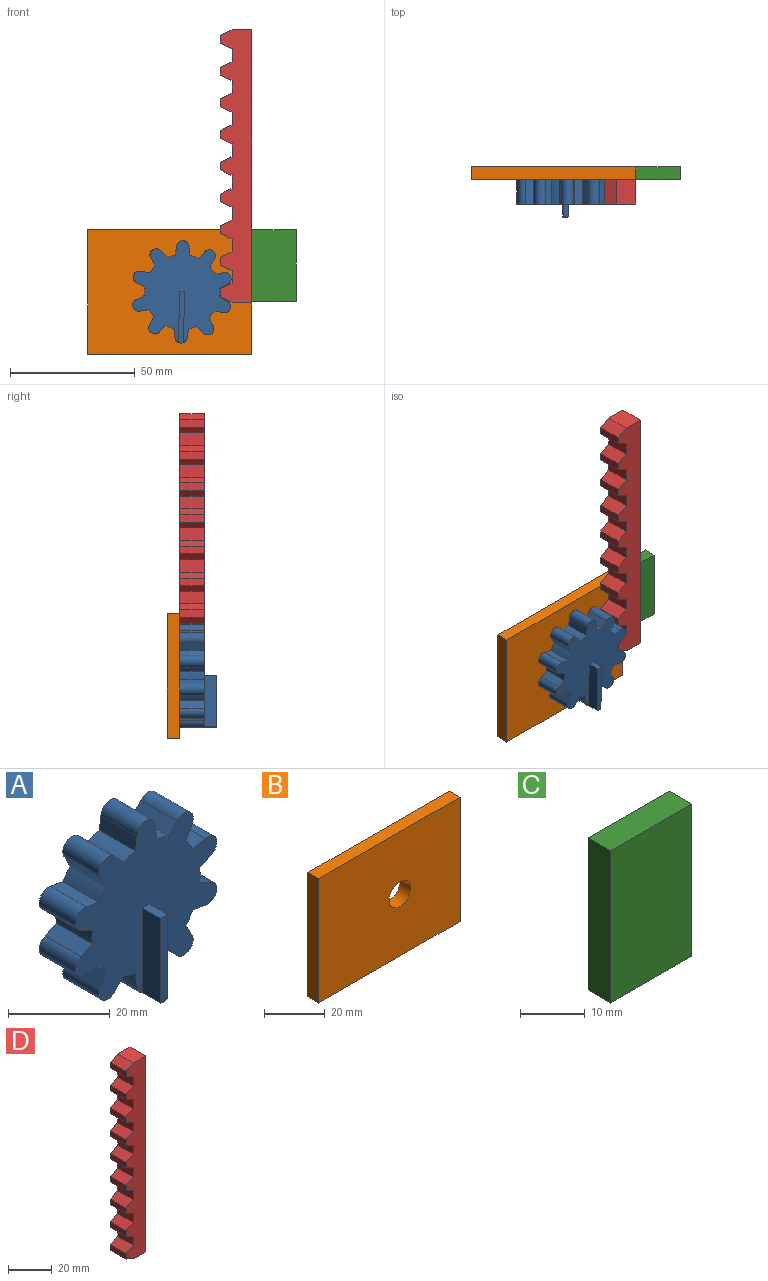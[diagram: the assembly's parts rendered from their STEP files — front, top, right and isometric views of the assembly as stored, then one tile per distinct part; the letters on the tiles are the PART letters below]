
ASSEMBLY  parts=4 mates=3
PART A: 46 faces, bbox 39.2x15x41 mm
  f0: plane 5x2mm, normal (0,0,1), area 10mm2, adj f1,f3,f4,f5
  f1: plane 20.29x5mm, normal (-1,0,0), area 101.5mm2, adj f0,f2,f4,f5
  f2: cylinder r=2.5mm len=15mm, axis (0,1,0), area 87.5mm2, adj f1,f3,f4,f5,f36,f37,f45
  f3: plane 20.29x5mm, normal (1,0,0), area 101.5mm2, adj f0,f2,f4,f5
  f4: plane 20.5x2mm, normal (0,-1,0), area 40.9mm2, adj f0,f1,f2,f3
  f5: plane 40.79x39.24mm, normal (0,-1,0), area 934.1mm2, adj f0,f1,f2,f3,f6,f7,f8,f9
  f6: plane 10x3.05mm, normal (0.45,0,0.9), area 34.1mm2, adj f5,f7,f44,f45
  f7: cylinder r=15mm len=10mm, axis (0,1,0), area 33.8mm2, adj f5,f6,f8,f45
  f8: plane 10x3.05mm, normal (0.45,0,-0.9), area 34.1mm2, adj f5,f7,f9,f45
  f9: cylinder r=2.5mm len=10mm, axis (0,1,0), area 77.2mm2, adj f5,f8,f10,f45
  f10: plane 10x3.36mm, normal (-0.17,0,0.99), area 34.1mm2, adj f5,f9,f11,f45
  f11: cylinder r=15mm len=10mm, axis (0,1,0), area 33.8mm2, adj f5,f10,f12,f45
  f12: plane 10x3.02mm, normal (0.89,0,-0.46), area 34.1mm2, adj f5,f11,f13,f45
  f13: cylinder r=2.5mm len=10mm, axis (0,1,0), area 77.2mm2, adj f5,f12,f14,f45
  f14: plane 10x2.43mm, normal (-0.71,0,0.7), area 34.1mm2, adj f5,f13,f15,f45
  f15: cylinder r=15mm len=10mm, axis (0,1,0), area 33.8mm2, adj f5,f14,f16,f45
  f16: plane 10x3.37mm, normal (0.99,0,0.15), area 34.1mm2, adj f5,f15,f17,f45
  f17: cylinder r=2.5mm len=10mm, axis (0,1,0), area 77.2mm2, adj f5,f16,f18,f45
  f18: plane 10x3.37mm, normal (-0.99,0,0.15), area 34.1mm2, adj f5,f17,f19,f45
  f19: cylinder r=15mm len=10mm, axis (0,1,0), area 33.8mm2, adj f5,f18,f20,f45
  f20: plane 10x2.43mm, normal (0.71,0,0.7), area 34.1mm2, adj f5,f19,f21,f45
  f21: cylinder r=2.5mm len=10mm, axis (0,1,0), area 77.2mm2, adj f5,f20,f22,f45
  f22: plane 10x3.02mm, normal (-0.89,0,-0.46), area 34.1mm2, adj f5,f21,f23,f45
  f23: cylinder r=15mm len=10mm, axis (0,1,0), area 33.8mm2, adj f5,f22,f24,f45
  f24: plane 10x3.36mm, normal (0.17,0,0.99), area 34.1mm2, adj f5,f23,f25,f45
  f25: cylinder r=2.5mm len=10mm, axis (0,1,0), area 77.2mm2, adj f5,f24,f26,f45
  f26: plane 10x3.05mm, normal (-0.45,0,-0.9), area 34.1mm2, adj f5,f25,f27,f45
  f27: cylinder r=15mm len=10mm, axis (0,1,0), area 33.8mm2, adj f5,f26,f28,f45
  f28: plane 10x3.05mm, normal (-0.45,0,0.9), area 34.1mm2, adj f5,f27,f29,f45
  f29: cylinder r=2.5mm len=10mm, axis (0,1,0), area 77.2mm2, adj f5,f28,f30,f45
  f30: plane 10x3.36mm, normal (0.17,0,-0.99), area 34.1mm2, adj f5,f29,f31,f45
  f31: cylinder r=15mm len=10mm, axis (0,1,0), area 33.8mm2, adj f5,f30,f32,f45
  f32: plane 10x3.02mm, normal (-0.89,0,0.46), area 34.1mm2, adj f5,f31,f33,f45
  f33: cylinder r=2.5mm len=10mm, axis (0,1,0), area 77.2mm2, adj f5,f32,f34,f45
  f34: plane 10x2.43mm, normal (0.71,0,-0.7), area 34.1mm2, adj f5,f33,f35,f45
  f35: cylinder r=15mm len=10mm, axis (0,1,0), area 33.8mm2, adj f5,f34,f36,f45
  f36: plane 10x3.37mm, normal (-0.99,0,-0.15), area 34.1mm2, adj f2,f5,f35,f45
  f37: plane 10x3.37mm, normal (0.99,0,-0.15), area 34.1mm2, adj f2,f5,f38,f45
  f38: cylinder r=15mm len=10mm, axis (0,1,0), area 33.8mm2, adj f5,f37,f39,f45
  f39: plane 10x2.43mm, normal (-0.71,0,-0.7), area 34.1mm2, adj f5,f38,f40,f45
  f40: cylinder r=2.5mm len=10mm, axis (0,1,0), area 77.2mm2, adj f5,f39,f41,f45
  f41: plane 10x3.02mm, normal (0.89,0,0.46), area 34.1mm2, adj f5,f40,f42,f45
  f42: cylinder r=15mm len=10mm, axis (0,1,0), area 33.8mm2, adj f5,f41,f43,f45
  f43: plane 10x3.36mm, normal (-0.17,0,-0.99), area 34.1mm2, adj f5,f42,f44,f45
  f44: cylinder r=2.5mm len=10mm, axis (0,1,0), area 77.2mm2, adj f5,f6,f43,f45
  f45: plane 41x39.24mm, normal (0,1,0), area 975mm2, adj f2,f6,f7,f8,f9,f10,f11,f12
PART B: 7 faces, bbox 65.7x5x50 mm
  f0: plane 65.72x5mm, normal (0,0,1), area 328.6mm2, adj f1,f3,f4,f6
  f1: plane 50x5mm, normal (-1,0,0), area 250mm2, adj f0,f2,f3,f4
  f2: plane 65.72x5mm, normal (0,0,-1), area 328.6mm2, adj f1,f3,f4,f6
  f3: plane 65.72x50mm, normal (0,1,0), area 3207.6mm2, adj f0,f1,f2,f5,f6
  f4: plane 65.72x50mm, normal (0,-1,0), area 3207.6mm2, adj f0,f1,f2,f5,f6
  f5: cylinder r=5mm len=10mm, axis (0,-1,0), area 157.1mm2, adj f3,f4
  f6: plane 50x5mm, normal (1,0,0), area 250mm2, adj f0,f2,f3,f4
PART C: 6 faces, bbox 17.8x5x28.9 mm
  f0: plane 28.85x5mm, normal (-1,0,0), area 144.2mm2, adj f1,f3,f4,f5
  f1: plane 17.77x5mm, normal (0,0,-1), area 88.9mm2, adj f0,f2,f4,f5
  f2: plane 28.85x5mm, normal (1,0,0), area 144.2mm2, adj f1,f3,f4,f5
  f3: plane 17.77x5mm, normal (0,0,1), area 88.9mm2, adj f0,f2,f4,f5
  f4: plane 28.85x17.77mm, normal (0,1,0), area 512.7mm2, adj f0,f1,f2,f3
  f5: plane 28.85x17.77mm, normal (0,-1,0), area 512.7mm2, adj f0,f1,f2,f3
PART D: 40 faces, bbox 12.6x10x109.3 mm
  f0: plane 10x4.61mm, normal (-0.45,0,-0.9), area 51.5mm2, adj f1,f19,f20,f21
  f1: plane 10x5mm, normal (-1,0,0), area 50mm2, adj f0,f2,f20,f21
  f2: plane 10x4.61mm, normal (-0.45,0,0.9), area 51.5mm2, adj f1,f3,f20,f21
  f3: plane 10x3.09mm, normal (-1,0,0), area 30.8mm2, adj f2,f4,f20,f21
  f4: plane 10x4.61mm, normal (-0.45,0,-0.9), area 51.5mm2, adj f3,f5,f20,f21
  f5: plane 10x5mm, normal (-1,0,0), area 50mm2, adj f4,f6,f20,f21
  f6: plane 10x4.61mm, normal (-0.45,0,0.9), area 51.5mm2, adj f5,f7,f20,f21
  f7: plane 10x3.11mm, normal (-1,0,0), area 31.1mm2, adj f6,f8,f20,f21
  f8: plane 10x4.61mm, normal (-0.45,0,-0.9), area 51.5mm2, adj f7,f9,f20,f21
  f9: plane 10x7.94mm, normal (0,0,-1), area 79.4mm2, adj f8,f10,f20,f21
  f10: plane 109.3x10mm, normal (1,0,0), area 1093mm2, adj f9,f20,f21,f29
  f11: plane 10x4.61mm, normal (-0.45,0,0.9), area 51.5mm2, adj f12,f20,f21,f28
  f12: plane 10x3.11mm, normal (-1,0,0), area 31.1mm2, adj f11,f20,f21,f22
  f13: plane 10x5.08mm, normal (-1,0,0), area 50.8mm2, adj f14,f20,f21,f22
  f14: plane 10x4.61mm, normal (-0.45,0,0.9), area 51.5mm2, adj f13,f15,f20,f21
  f15: plane 10x3.09mm, normal (-1,0,0), area 30.8mm2, adj f14,f16,f20,f21
  f16: plane 10x4.61mm, normal (-0.45,0,-0.9), area 51.5mm2, adj f15,f17,f20,f21
  f17: plane 10x5mm, normal (-1,0,0), area 50mm2, adj f16,f18,f20,f21
  f18: plane 10x4.61mm, normal (-0.45,0,0.9), area 51.5mm2, adj f17,f19,f20,f21
  f19: plane 10x3.09mm, normal (-1,0,0), area 30.8mm2, adj f0,f18,f20,f21
  f20: plane 109.3x12.56mm, normal (0,-1,0), area 1091.6mm2, adj f0,f1,f2,f3,f4,f5,f6,f7
  f21: plane 109.3x12.56mm, normal (0,1,0), area 1091.6mm2, adj f0,f1,f2,f3,f4,f5,f6,f7
  f22: plane 10x4.61mm, normal (-0.45,0,-0.9), area 51.5mm2, adj f12,f13,f20,f21
  f23: plane 10x4.61mm, normal (-0.45,0,-0.9), area 51.5mm2, adj f20,f21,f24,f39
  f24: plane 10x5mm, normal (-1,0,0), area 50mm2, adj f20,f21,f23,f25
  f25: plane 10x4.61mm, normal (-0.45,0,0.9), area 51.5mm2, adj f20,f21,f24,f26
  f26: plane 10x3.09mm, normal (-1,0,0), area 30.8mm2, adj f20,f21,f25,f27
  f27: plane 10x4.61mm, normal (-0.45,0,-0.9), area 51.5mm2, adj f20,f21,f26,f28
  f28: plane 10x5mm, normal (-1,0,0), area 50mm2, adj f11,f20,f21,f27
  f29: plane 10x7.94mm, normal (0,0,1), area 79.4mm2, adj f10,f20,f21,f30
  f30: plane 10x4.61mm, normal (-0.45,0,0.9), area 51.5mm2, adj f20,f21,f29,f31
  f31: plane 10x3.09mm, normal (-1,0,0), area 30.8mm2, adj f20,f21,f30,f32
  f32: plane 10x4.61mm, normal (-0.45,0,-0.9), area 51.5mm2, adj f20,f21,f31,f33
  f33: plane 10x5.11mm, normal (-1,0,0), area 51.1mm2, adj f20,f21,f32,f34
  f34: plane 10x4.61mm, normal (-0.45,0,0.9), area 51.5mm2, adj f20,f21,f33,f35
  f35: plane 10x3.09mm, normal (-1,0,0), area 30.8mm2, adj f20,f21,f34,f36
  f36: plane 10x4.61mm, normal (-0.45,0,-0.9), area 51.5mm2, adj f20,f21,f35,f37
  f37: plane 10x5mm, normal (-1,0,0), area 50mm2, adj f20,f21,f36,f38
  f38: plane 10x4.61mm, normal (-0.45,0,0.9), area 51.5mm2, adj f20,f21,f37,f39
  f39: plane 10x3.09mm, normal (-1,0,0), area 30.8mm2, adj f20,f21,f23,f38
PLACE A rot(axis=(0,1,0),1deg) t=(-0.39,3.32,-10.14)mm
PLACE B t=(-0.39,3.32,-10.14)mm fixed
PLACE C t=(-0.39,3.32,-10.14)mm
PLACE D t=(-0.39,3.32,-10.5)mm
MATE fastened C.f3 <-> B.f0  axis (0,0,1) through (27.61,3.32,14.86)mm
MATE slider D.f9 <-> C.f1  axis (0,0,-1) through (27.61,3.32,-14.35)mm
MATE revolute B.f5 <-> A.f7  axis (0,-1,0) through (-0.39,3.32,-10.14)mm
